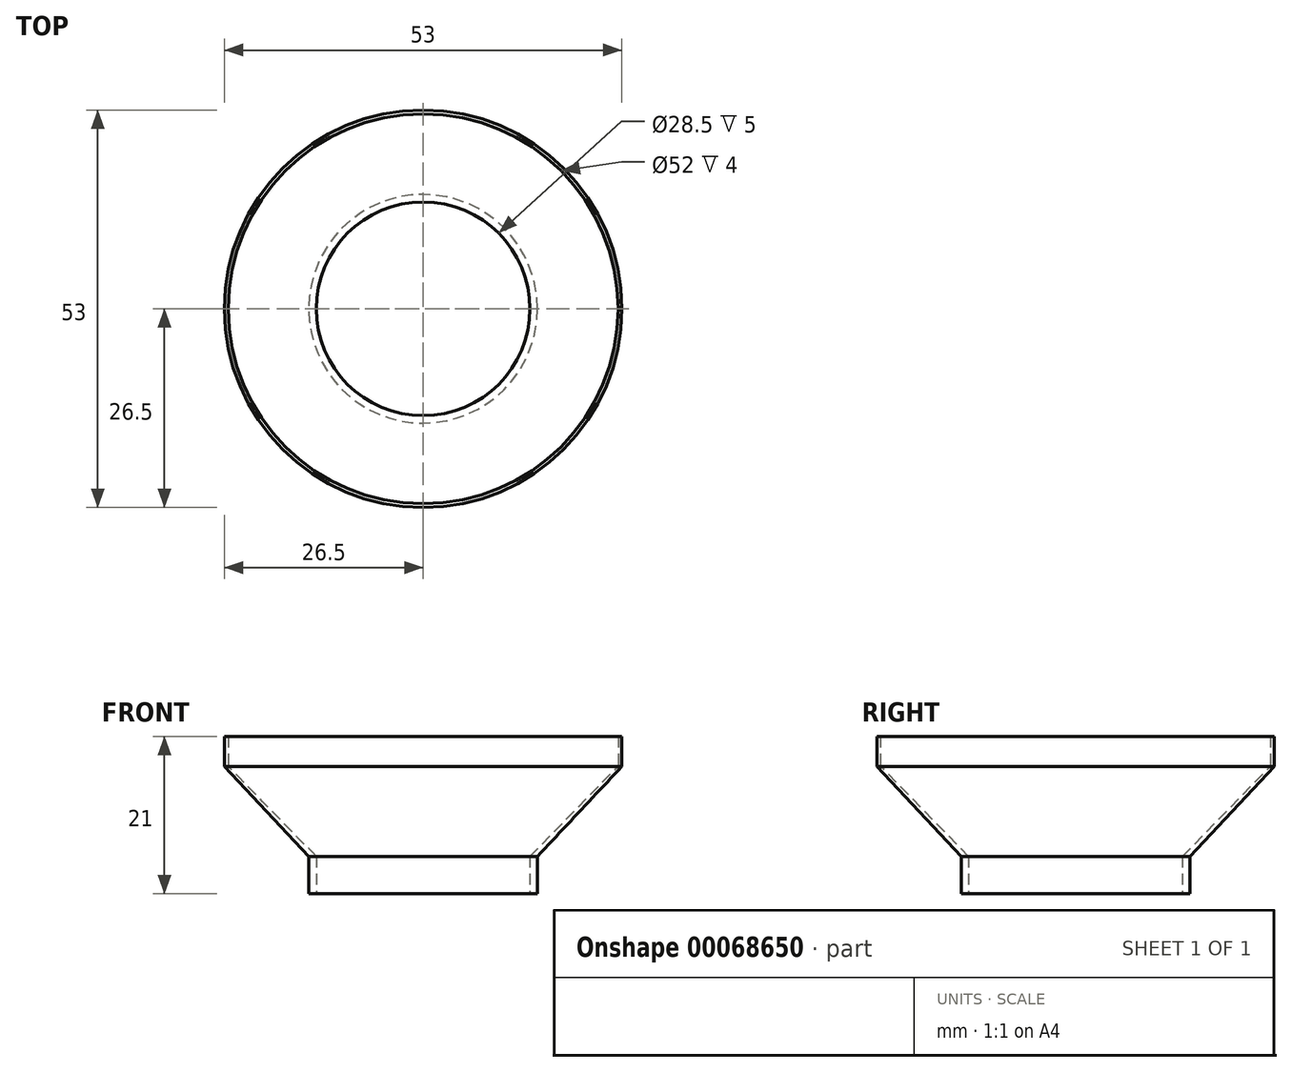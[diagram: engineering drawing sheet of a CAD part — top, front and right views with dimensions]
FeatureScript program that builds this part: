
annotation { "Feature Type Name" : "Feature", "Feature Type Description" : "" }
export const myFeature = defineFeature(function(context is Context, id is Id, definition is map)
    precondition{}
    {
        {
            var Q0;
            Q0=qCreatedBy(makeId("Top.planeOp"),FACE);
            var sketch = newSketch(context, id + "F0", { "sketchPlane" : qUnion([Q0])});
            skCircle(sketch, "E0", {"center": v(0, 0) * mm, "radius": 14.25 * mm});
            skCircle(sketch, "E1", {"center": v(0, 0) * mm, "radius": 15.25 * mm});
            skLineSegment(sketch, "E2", {"start": v(0, 14.25) * mm, "end": v(0, 15.25) * mm, "construction": true});
            skLineSegment(sketch, "E3", {"start": v(-15.25, 0) * mm, "end": v(-14.25, 0) * mm});
            skLineSegment(sketch, "E4", {"start": v(14.25, 0) * mm, "end": v(15.25, 0) * mm});
            skSolve(sketch);
        }
        {
            var Q0;
            {var subQ0=sQuery(id+"F0.wireOp",EDGE,"E3");Q0=makeQuery(id+"F0.imprint","IMPRINT",FACE,{"disambiguationData":[TD([[makeQuery(id+"F0.imprint","IMPRINT",EDGE,{"derivedFrom":subQ0}),1.0]])]});}
            var Q1;
            {var subQ0=sQuery(id+"F0.wireOp",EDGE,"E3");Q1=makeQuery(id+"F0.imprint","IMPRINT",FACE,{"disambiguationData":[TD([[makeQuery(id+"F0.imprint","IMPRINT",EDGE,{"derivedFrom":subQ0}),-1.0]])]});}
            extrude(context, id + "F1", {"entities" : qUnion([Q0, Q1]), "depth" : 5 * mm});
        }
        {
            var Q0;
            Q0=makeQuery(id+"F1.opExtrude","CAP_FACE",FACE,{"disambiguationData":[OSD([sQuery(id+"F0.wireOp",EDGE,"E0"),sQuery(id+"F0.wireOp",EDGE,"E1")])],"isStart":false});
            cPlane(context, id + "F2", {"entities" : qUnion([Q0]), "cplaneType" : CPlaneType.OFFSET, "offset" : 12 * mm, "width" : 150 * mm, "height" : 150 * mm});
        }
        {
            var Q0;
            Q0=qCreatedBy(id+"F2.planeOp",FACE);
            var sketch = newSketch(context, id + "F3", { "sketchPlane" : qUnion([Q0])});
            skCircle(sketch, "E5", {"center": v(0, 0) * mm, "radius": 26 * mm});
            skCircle(sketch, "E6", {"center": v(0, 0) * mm, "radius": 26.5 * mm});
            skSolve(sketch);
        }
        {
            var Q0;
            Q0=qCreatedBy(makeId("Front.planeOp"),FACE);
            var sketch = newSketch(context, id + "F4", { "sketchPlane" : qUnion([Q0])});
            skLineSegment(sketch, "E7.0", {"start": v(-14.25, 5) * mm, "end": v(14.25, 5) * mm});
            skLineSegment(sketch, "E8.0", {"start": v(-15.25, 5) * mm, "end": v(15.25, 5) * mm});
            skLineSegment(sketch, "E9", {"start": v(-26, 17) * mm, "end": v(-14.25, 5) * mm});
            skLineSegment(sketch, "E10.0", {"start": v(-26.5, 17) * mm, "end": v(26.5, 17) * mm});
            skLineSegment(sketch, "E11", {"start": v(-26.5, 17) * mm, "end": v(-15.25, 5) * mm});
            skLineSegment(sketch, "E12", {"start": v(-26, 17) * mm, "end": v(-26.5, 17) * mm});
            skLineSegment(sketch, "E13", {"start": v(0, 5) * mm, "end": v(0, 66.26) * mm, "construction": true});
            skPoint(sketch, "E13.endSnap0", {"position": v(0, 17) * mm});
            skSolve(sketch);
        }
        {
            var Q0;
            {var subQ2=sQuery(id+"F4.wireOp",EDGE,"E9");Q0=makeQuery(id+"F4.imprint","IMPRINT",FACE,{"disambiguationData":[TD([[makeQuery(id+"F4.imprint","IMPRINT",EDGE,{"derivedFrom":subQ2}),-1.0]])]});}
            var Q1;
            Q1=sQuery(id+"F4.wireOp",EDGE,"E13");
            revolve(context, id + "F5", {"operationType" : NewBodyOperationType.ADD, "entities" : qUnion([Q0]), "axis" : qUnion([Q1]), "revolveType" : RevolveType.FULL});
        }
        {
            var Q0;
            Q0=makeQuery(id+"F3.imprint","IMPRINT",FACE,{"disambiguationData":[TD([[makeQuery(id+"F3.imprint","IMPRINT",EDGE,{"derivedFrom":sQuery(id+"F3.wireOp",EDGE,"E5")}),-1.0]])]});
            extrude(context, id + "F6", {"entities" : qUnion([Q0]), "operationType" : NewBodyOperationType.ADD, "depth" : 4 * mm});
        }
    });
